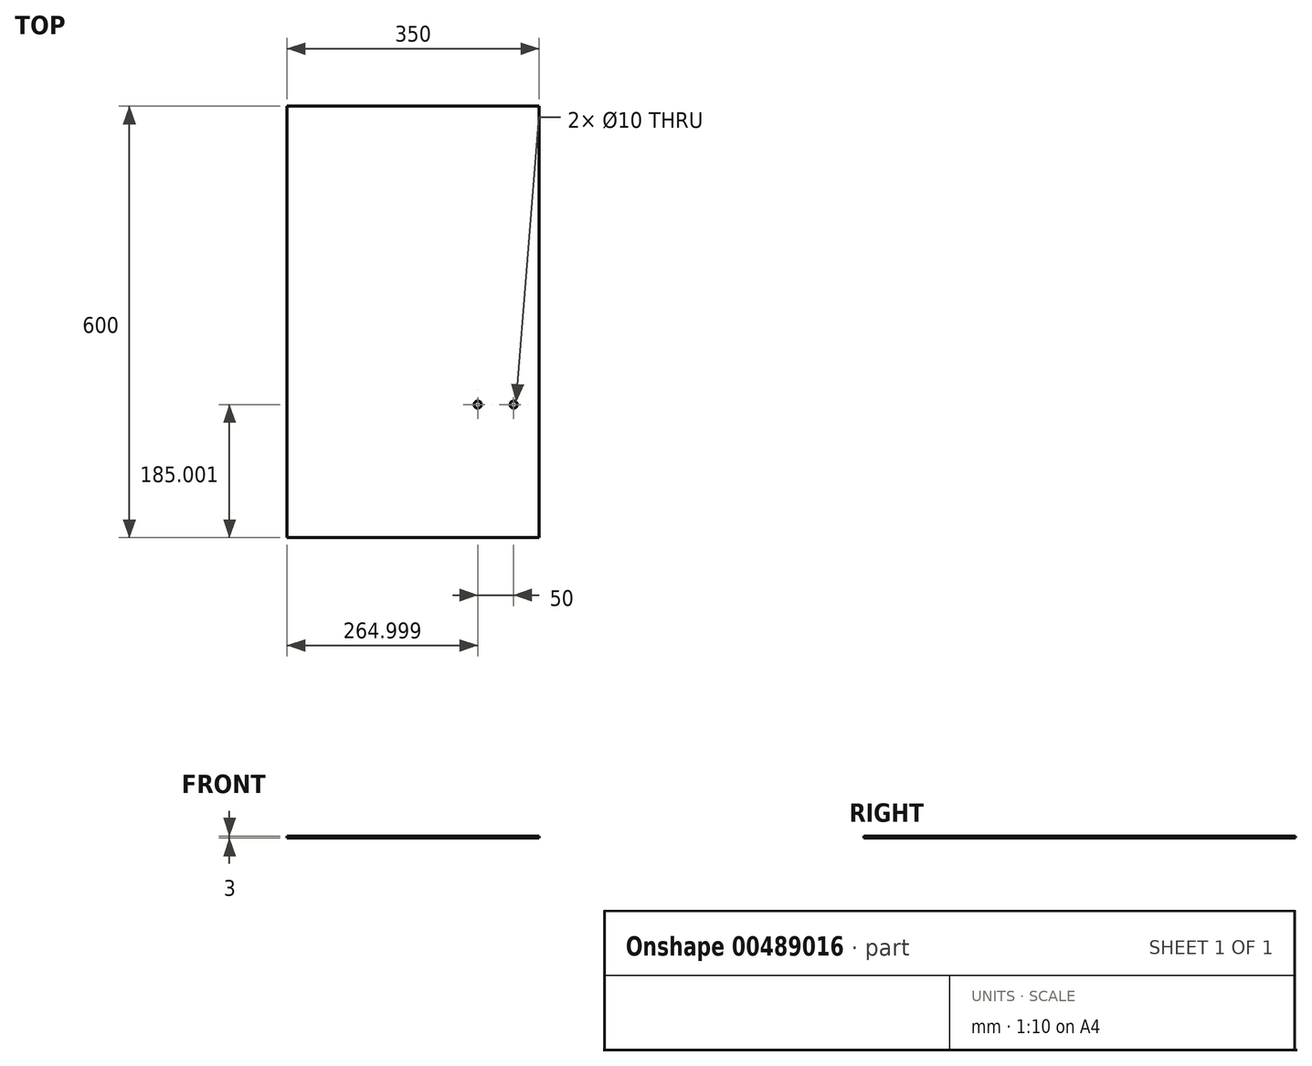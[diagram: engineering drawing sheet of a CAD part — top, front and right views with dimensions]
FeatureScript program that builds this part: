
annotation { "Feature Type Name" : "Feature", "Feature Type Description" : "" }
export const myFeature = defineFeature(function(context is Context, id is Id, definition is map)
    precondition{}
    {
        {
            var Q0;
            Q0=qCreatedBy(makeId("Top.planeOp"),FACE);
            var sketch = newSketch(context, id + "F0", { "sketchPlane" : qUnion([Q0])});
            skLineSegment(sketch, "E0.bottom", {"start": v(-182.31, 203.11) * mm, "end": v(167.69, 203.11) * mm});
            skLineSegment(sketch, "E0.top", {"start": v(-182.31, -396.89) * mm, "end": v(167.69, -396.89) * mm});
            skLineSegment(sketch, "E0.left", {"start": v(-182.31, 203.11) * mm, "end": v(-182.31, -396.89) * mm});
            skLineSegment(sketch, "E0.right", {"start": v(167.69, 203.11) * mm, "end": v(167.69, -396.89) * mm});
            skSolve(sketch);
        }
        {
            var Q0;
            Q0 = qSketchRegion(id + "F0", true);
            extrude(context, id + "F1", {"entities" : qUnion([Q0]), "depth" : 3 * mm});
        }
        {
            var Q0;
            Q0=makeQuery(id+"F1.opExtrude","CAP_FACE",FACE,{"disambiguationData":[OSD([sQuery(id+"F0.wireOp",EDGE,"E0.bottom"),sQuery(id+"F0.wireOp",EDGE,"E0.top"),sQuery(id+"F0.wireOp",EDGE,"E0.left"),sQuery(id+"F0.wireOp",EDGE,"E0.right")])],"isStart":false});
            var sketch = newSketch(context, id + "F2", { "sketchPlane" : qUnion([Q0])});
            skCircle(sketch, "E1", {"center": v(82.69, -211.89) * mm, "radius": 5 * mm});
            skCircle(sketch, "E2", {"center": v(132.69, -211.89) * mm, "radius": 5 * mm});
            skSolve(sketch);
        }
        {
            var Q0;
            Q0 = qSketchRegion(id + "F2", true);
            extrude(context, id + "F3", {"entities" : qUnion([Q0]), "operationType" : NewBodyOperationType.REMOVE, "oppositeDirection" : true, "depth" : 3 * mm, "offsetDistance" : 25 * mm});
        }
    });
